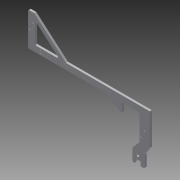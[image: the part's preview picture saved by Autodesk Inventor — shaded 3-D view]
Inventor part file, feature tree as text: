
AUTODESK INVENTOR PART (.ipt)
format: ipt  version: 2014 SP1 (Build 180222100, 222)  size: 223,232 bytes
history: native  units: in
note: dims shown in document units (in); Inventor stores cm internally (conversion verified against a paired STEP export)
features: extrude x4, fillet x3, sketch x3, plane x2
ambient origin geometry x8: Origin, YZ Plane, XZ Plane, XY Plane, X Axis, Y Axis, Z Axis, Center Point
bodies: Body1 (feature_tree)
feature tree (12):
  plane  "Work Plane4"
  plane  "Work Plane3"
  extrude  "Extrusion9"  Depth=1.25in
  extrude  "Extrusion10"  Depth=0.125in
  extrude  "Extrusion11"  Depth=0.75in
  fillet  "Fillet8"  Radius=1.5in
  fillet  "Fillet9"  [1 undecoded]
  extrude  "Extrusion13"  Depth=2.15in
  fillet  "Fillet11"  Radius=0.875in
  sketch  "Sketch8"  dims[d0=0.25in d1=0.5in d2=0.75in d3=0.25in d4=0.5in d5=0.3765in d6=0.5in d8=14.875in d17=4.0833in d19=0.375in d25=1.25in]
  sketch  "Sketch9"  dims[d26=0.125in d27=2.0in]
  sketch  "Sketch11"  dims[d28=1.0in d29=1.0in d30=0.75in d63=1.5in d68=0.0in d69=2.15in d71=0.875in d72=0.0in d73=6.625in d74=3.125in d76=9.475in d87=0.25in d88=1.5in d89=1.0in d91=1.0in d93=0.2797in d94=0.5in d97=0.2797in d98=10.5406in d99=0.25in d100=0.0in d101=0.15in d102=0.15in d104=1.113in d105=0.175in d107=0.25in d108=0.0in d109=0.125in d110=0.125in d111=1.5in d112=1.5in d113=0.25in d114=0.25in d115=0.125in d116=0.125in d117=1.5in d118=1.5in d119=0.1875in d121=0.25in d122=0.0in d123=0.125in d124=0.3125in d125=0.125in d135=1.0in d136=1.0in d139=0.25in d140=1.0in d141=0.0in d143=0.85in d144=0.25in d145=0.125in d147=0.8543in d148=0.4055in d149=0.15in d150=0.15in d151=0.8543in d152=0.4055in d153=1.625in d154=0.175in]
note: 1 required parameter value undecoded (feature->parameter linkage not recoverable at this tier; creation-order binding heuristic only, values carry confidence <= 0.55)
